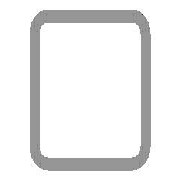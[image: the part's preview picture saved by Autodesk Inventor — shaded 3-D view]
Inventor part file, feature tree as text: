
AUTODESK INVENTOR PART (.ipt)
format: ipt  version: 2025.1 (Build 291241020, 241B)  size: 144,896 bytes
history: native  units: mm (DEFAULTED — no unit token found)
features: other x4, sketch x1, plane x1
ambient origin geometry x8: Origin, YZ Plane, XZ Plane, XY Plane, X Axis, Y Axis, Z Axis, Center Point
bodies: Solid1 (feature_tree), Body (feature_tree)
feature tree (6):
  parser-record x1  (decoder bookkeeping rows leaked as tree rows — omitted from the tree; the rows remain in map.json)
  other  "Driven Length"
  other  "Start plane"
  other  "End plane"
  sketch  "Sketch3"  dims[d3=7000.0mm d4=0.0mm d7=6.0mm d9=100.0mm d11=100.0mm d12=3.0mm d13=-0.0mm d14=7000.0mm d15=50.0mm d16=50.0mm d17=90.0deg d18=7000.0mm]
  plane  "Work Plane3"
